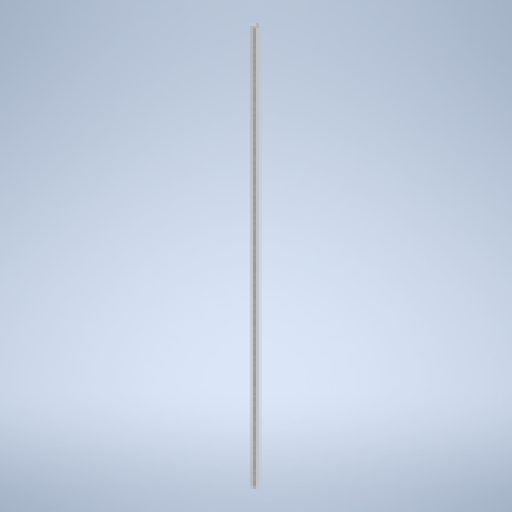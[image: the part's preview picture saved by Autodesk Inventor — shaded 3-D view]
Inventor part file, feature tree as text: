
AUTODESK INVENTOR PART (.ipt)
format: ipt  version: 2024 (Build 280153000, 153)  size: 406,016 bytes
history: native  units: in
note: dims shown in document units (in); Inventor stores cm internally (conversion verified against a paired STEP export)
features: extrude x2, pattern_linear x1, sketch x1
ambient origin geometry x8: Origin, YZ Plane, XZ Plane, XY Plane, X Axis, Y Axis, Z Axis, Center Point
bodies: Body1 (feature_tree)
feature tree (4):
  extrude  "Extrusion2"  Depth=1.0in
  extrude  "Extrusion3"  Depth=0.09in
  pattern_linear  "Rectangular Pattern1"  Spacing1=94.0in  [1 undecoded]
  sketch  "Sketch5"  dims[d13=1.0in d14=1.0in d15=0.09in d16=94.0in d17=0.0in d18=0.201in d19=0.5in d20=0.5in d21=0.0in d22=0.0in d23=37.0079in d25=1.0in]
note: 1 required parameter value undecoded (feature->parameter linkage not recoverable at this tier; creation-order binding heuristic only, values carry confidence <= 0.55)
